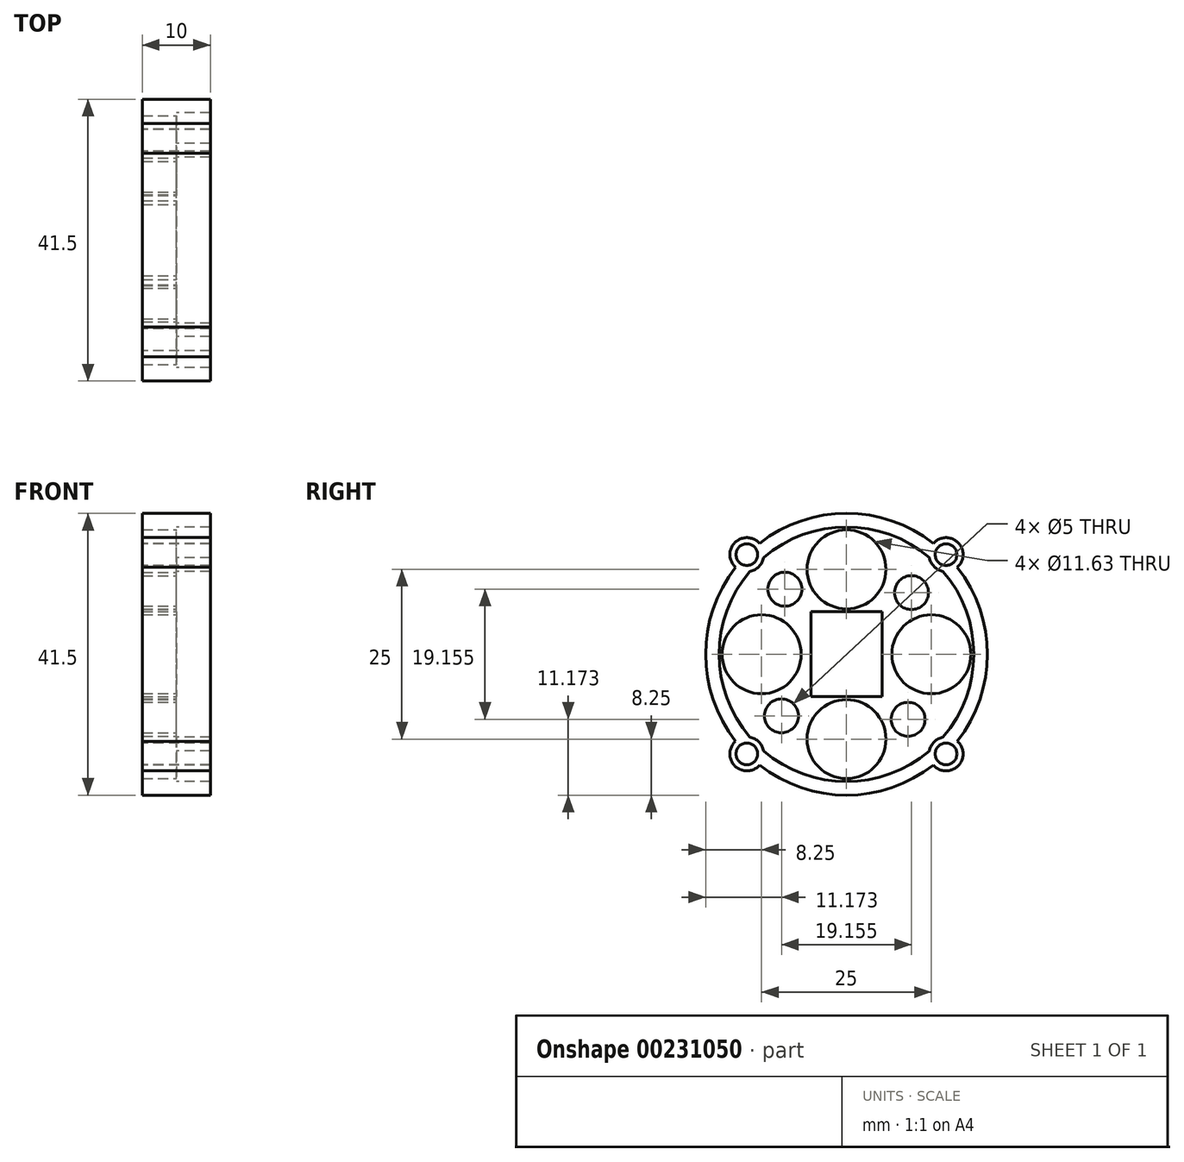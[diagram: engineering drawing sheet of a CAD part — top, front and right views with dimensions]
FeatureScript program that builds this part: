
annotation { "Feature Type Name" : "Feature", "Feature Type Description" : "" }
export const myFeature = defineFeature(function(context is Context, id is Id, definition is map)
    precondition{}
    {
        {
            var Q0;
            Q0=qCreatedBy(makeId("Right.planeOp"),FACE);
            var sketch = newSketch(context, id + "F0", { "sketchPlane" : qUnion([Q0])});
            skLineSegment(sketch, "E0.bottom", {"start": v(20.75, 20.75) * mm, "end": v(-20.75, 20.75) * mm});
            skLineSegment(sketch, "E0.top", {"start": v(20.75, -20.75) * mm, "end": v(-20.75, -20.75) * mm});
            skLineSegment(sketch, "E0.left", {"start": v(20.75, 20.75) * mm, "end": v(20.75, -20.75) * mm});
            skLineSegment(sketch, "E0.right", {"start": v(-20.75, 20.75) * mm, "end": v(-20.75, -20.75) * mm});
            skArc(sketch, "E1", {"start": v(12.21, 14.23) * mm, "mid": v(0, 18.75) * mm, "end": v(-12.21, 14.23) * mm});
            skArc(sketch, "E2", {"start": v(12.8, 16.33) * mm, "mid": v(0, 20.75) * mm, "end": v(-12.8, 16.33) * mm});
            skLineSegment(sketch, "E3", {"start": v(0, 0) * mm, "end": v(20.75, 20.75) * mm});
            skArc(sketch, "E4", {"start": v(12.21, 14.23) * mm, "mid": v(12.9, 12.9) * mm, "end": v(14.23, 12.21) * mm});
            skCircle(sketch, "E5", {"center": v(14.67, 14.67) * mm, "radius": 1.6 * mm});
            skArc(sketch, "E6.trimOffspring", {"start": v(16.33, 12.8) * mm, "mid": v(16.44, 16.44) * mm, "end": v(12.8, 16.33) * mm});
            skArc(sketch, "E7.1.0", {"start": v(-12.8, 16.33) * mm, "mid": v(-16.44, 16.44) * mm, "end": v(-16.33, 12.8) * mm});
            skCircle(sketch, "E7.1.1", {"center": v(-14.67, 14.67) * mm, "radius": 1.6 * mm});
            skArc(sketch, "E7.1.2", {"start": v(-14.23, 12.21) * mm, "mid": v(-12.9, 12.9) * mm, "end": v(-12.21, 14.23) * mm});
            skArc(sketch, "E7.2.0", {"start": v(-16.33, -12.8) * mm, "mid": v(-16.44, -16.44) * mm, "end": v(-12.8, -16.33) * mm});
            skCircle(sketch, "E7.2.1", {"center": v(-14.67, -14.67) * mm, "radius": 1.6 * mm});
            skArc(sketch, "E7.2.2", {"start": v(-12.21, -14.23) * mm, "mid": v(-12.9, -12.9) * mm, "end": v(-14.23, -12.21) * mm});
            skArc(sketch, "E7.3.0", {"start": v(12.8, -16.33) * mm, "mid": v(16.44, -16.44) * mm, "end": v(16.33, -12.8) * mm});
            skCircle(sketch, "E7.3.1", {"center": v(14.67, -14.67) * mm, "radius": 1.6 * mm});
            skArc(sketch, "E7.3.2", {"start": v(14.23, -12.21) * mm, "mid": v(12.9, -12.9) * mm, "end": v(12.21, -14.23) * mm});
            skArc(sketch, "E8.trimOffspring", {"start": v(14.23, -12.21) * mm, "mid": v(18.75, 0) * mm, "end": v(14.23, 12.21) * mm});
            skArc(sketch, "E9.trimOffspring", {"start": v(16.33, -12.8) * mm, "mid": v(20.75, 0) * mm, "end": v(16.33, 12.8) * mm});
            skArc(sketch, "E10.trimOffspring", {"start": v(-12.21, -14.23) * mm, "mid": v(0, -18.75) * mm, "end": v(12.21, -14.23) * mm});
            skArc(sketch, "E11.trimOffspring", {"start": v(-12.8, -16.33) * mm, "mid": v(0, -20.75) * mm, "end": v(12.8, -16.33) * mm});
            skArc(sketch, "E12.trimOffspring", {"start": v(-16.33, 12.8) * mm, "mid": v(-20.75, 0) * mm, "end": v(-16.33, -12.8) * mm});
            skArc(sketch, "E13.trimOffspring", {"start": v(-14.23, 12.21) * mm, "mid": v(-18.75, 0) * mm, "end": v(-14.23, -12.21) * mm});
            skSolve(sketch);
        }
        {
            var Q0;
            {var subQ11=sQuery(id+"F0.wireOp",EDGE,"E1");Q0=makeQuery(id+"F0.imprint","IMPRINT",FACE,{"disambiguationData":[TD([[makeQuery(id+"F0.imprint","IMPRINT",EDGE,{"derivedFrom":subQ11}),-1.0]])]});}
            extrude(context, id + "F1", {"entities" : qUnion([Q0]), "depth" : 5 * mm});
        }
        {
            var Q0;
            Q0=makeQuery(id+"F1.opExtrude","CAP_FACE",FACE,{"disambiguationData":[OSD([sQuery(id+"F0.wireOp",EDGE,"E0.bottom"),sQuery(id+"F0.wireOp",EDGE,"E0.top"),sQuery(id+"F0.wireOp",EDGE,"E0.left"),sQuery(id+"F0.wireOp",EDGE,"E0.right"),sQuery(id+"F0.wireOp",EDGE,"E1")])],"isStart":true});
            var sketch = newSketch(context, id + "F2", { "sketchPlane" : qUnion([Q0])});
            skLineSegment(sketch, "E14.bottom", {"start": v(20.75, 20.75) * mm, "end": v(-20.75, 20.75) * mm});
            skLineSegment(sketch, "E14.top", {"start": v(20.75, -20.75) * mm, "end": v(-20.75, -20.75) * mm});
            skLineSegment(sketch, "E14.left", {"start": v(20.75, 20.75) * mm, "end": v(20.75, -20.75) * mm});
            skLineSegment(sketch, "E14.right", {"start": v(-20.75, 20.75) * mm, "end": v(-20.75, -20.75) * mm});
            skPoint(sketch, "E14.middle", {"position": v(0, 0) * mm});
            skLineSegment(sketch, "E15.bottom", {"start": v(5.25, 6.25) * mm, "end": v(-5.25, 6.25) * mm});
            skLineSegment(sketch, "E15.top", {"start": v(5.25, -6.25) * mm, "end": v(-5.25, -6.25) * mm});
            skLineSegment(sketch, "E15.left", {"start": v(5.25, 6.25) * mm, "end": v(5.25, -6.25) * mm});
            skLineSegment(sketch, "E15.right", {"start": v(-5.25, 6.25) * mm, "end": v(-5.25, -6.25) * mm});
            skArc(sketch, "E16", {"start": v(12.77, 16.35) * mm, "mid": v(0, 20.75) * mm, "end": v(-12.77, 16.35) * mm});
            skLineSegment(sketch, "E17", {"start": v(0, 0) * mm, "end": v(14.67, 14.67) * mm});
            skArc(sketch, "E18", {"start": v(16.35, 12.77) * mm, "mid": v(16.47, 16.47) * mm, "end": v(12.77, 16.35) * mm});
            skCircle(sketch, "E19", {"center": v(14.67, 14.67) * mm, "radius": 1.58 * mm});
            skArc(sketch, "E20.1.0", {"start": v(-12.77, 16.35) * mm, "mid": v(-16.47, 16.47) * mm, "end": v(-16.35, 12.77) * mm});
            skCircle(sketch, "E20.1.1", {"center": v(-14.67, 14.67) * mm, "radius": 1.58 * mm});
            skArc(sketch, "E20.2.0", {"start": v(-16.35, -12.77) * mm, "mid": v(-16.47, -16.47) * mm, "end": v(-12.77, -16.35) * mm});
            skCircle(sketch, "E20.2.1", {"center": v(-14.67, -14.67) * mm, "radius": 1.58 * mm});
            skArc(sketch, "E20.3.0", {"start": v(12.77, -16.35) * mm, "mid": v(16.47, -16.47) * mm, "end": v(16.35, -12.77) * mm});
            skCircle(sketch, "E20.3.1", {"center": v(14.67, -14.67) * mm, "radius": 1.58 * mm});
            skArc(sketch, "E21.trimOffspring", {"start": v(-16.35, 12.77) * mm, "mid": v(-20.75, 0) * mm, "end": v(-16.35, -12.77) * mm});
            skArc(sketch, "E22.trimOffspring", {"start": v(16.35, -12.77) * mm, "mid": v(20.75, 0) * mm, "end": v(16.35, 12.77) * mm});
            skArc(sketch, "E23.trimOffspring", {"start": v(-12.77, -16.35) * mm, "mid": v(0, -20.75) * mm, "end": v(12.77, -16.35) * mm});
            skSolve(sketch);
        }
        {
            var Q0;
            {var subQ30=makeQuery(id+"F1.opExtrude","CAP_EDGE",EDGE,{"disambiguationData":[OSD([sQuery(id+"F0.wireOp",EDGE,"E1")])],"isStart":true});Q0=makeQuery(id+"F2.imprint","IMPRINT",FACE,{"disambiguationData":[TD([[makeQuery(id+"F2.imprint","IMPRINT",EDGE,{"derivedFrom":subQ30}),1.0]])]});}
            var Q1;
            {var subQ4=sQuery(id+"F2.wireOp",EDGE,"E15.bottom");Q1=makeQuery(id+"F2.imprint","IMPRINT",FACE,{"disambiguationData":[TD([[makeQuery(id+"F2.imprint","IMPRINT",EDGE,{"derivedFrom":subQ4}),-1.0]])]});}
            extrude(context, id + "F3", {"entities" : qUnion([Q0, Q1]), "operationType" : NewBodyOperationType.ADD, "depth" : 5 * mm});
        }
        {
            var Q0;
            Q0=makeQuery(id+"F3.opExtrude","CAP_FACE",FACE,{"disambiguationData":[OSD([sQuery(id+"F0.wireOp",EDGE,"E2"),sQuery(id+"F0.wireOp",EDGE,"E5"),sQuery(id+"F0.wireOp",EDGE,"E6.trimOffspring"),sQuery(id+"F0.wireOp",EDGE,"E7.1.0"),sQuery(id+"F0.wireOp",EDGE,"E7.1.1"),sQuery(id+"F0.wireOp",EDGE,"E7.2.0"),sQuery(id+"F0.wireOp",EDGE,"E7.2.1"),sQuery(id+"F0.wireOp",EDGE,"E7.3.0"),sQuery(id+"F0.wireOp",EDGE,"E7.3.1"),sQuery(id+"F0.wireOp",EDGE,"E9.trimOffspring"),sQuery(id+"F0.wireOp",EDGE,"E11.trimOffspring"),sQuery(id+"F0.wireOp",EDGE,"E12.trimOffspring"),sQuery(id+"F2.wireOp",EDGE,"E15.bottom"),sQuery(id+"F2.wireOp",EDGE,"E15.top"),sQuery(id+"F2.wireOp",EDGE,"E15.left"),sQuery(id+"F2.wireOp",EDGE,"E15.right"),sQuery(id+"F2.wireOp",EDGE,"E16"),sQuery(id+"F2.wireOp",EDGE,"E21.trimOffspring"),sQuery(id+"F2.wireOp",EDGE,"E22.trimOffspring"),sQuery(id+"F2.wireOp",EDGE,"E23.trimOffspring")])],"isStart":true});
            var sketch = newSketch(context, id + "F4", { "sketchPlane" : qUnion([Q0])});
            skLineSegment(sketch, "E24", {"start": v(0, -6.25) * mm, "end": v(0, -18.75) * mm});
            skCircle(sketch, "E25", {"center": v(0, -12.5) * mm, "radius": 5.81 * mm});
            skLineSegment(sketch, "E26", {"start": v(5.25, -6.25) * mm, "end": v(12.9, -12.9) * mm});
            skCircle(sketch, "E27", {"center": v(9.08, -9.58) * mm, "radius": 2.5 * mm});
            skCircle(sketch, "E28.1.0", {"center": v(9.58, 9.08) * mm, "radius": 2.5 * mm});
            skCircle(sketch, "E28.1.1", {"center": v(12.5, 0) * mm, "radius": 5.81 * mm});
            skCircle(sketch, "E28.2.0", {"center": v(-9.08, 9.58) * mm, "radius": 2.5 * mm});
            skCircle(sketch, "E28.2.1", {"center": v(0, 12.5) * mm, "radius": 5.81 * mm});
            skCircle(sketch, "E28.3.0", {"center": v(-9.58, -9.08) * mm, "radius": 2.5 * mm});
            skCircle(sketch, "E28.3.1", {"center": v(-12.5, 0) * mm, "radius": 5.81 * mm});
            skPoint(sketch, "E28.center", {"position": v(0, 0) * mm});
            skSolve(sketch);
        }
        {
            var Q0;
            Q0 = qSketchRegion(id + "F4", true);
            extrude(context, id + "F5", {"entities" : qUnion([Q0]), "operationType" : NewBodyOperationType.REMOVE, "endBound" : BoundingType.THROUGH_ALL, "oppositeDirection" : true, "depth" : 25 * mm});
        }
    });
